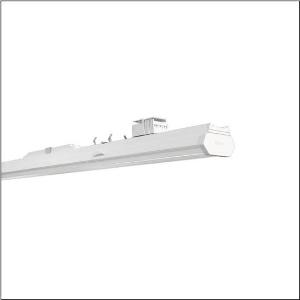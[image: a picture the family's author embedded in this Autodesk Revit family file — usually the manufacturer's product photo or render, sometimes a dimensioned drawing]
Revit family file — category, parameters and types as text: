
# Revit family: licross_21_protected_mo_52td11cn49xg
name_source: partatom
category: Lighting Fixtures
units: mm (PartAtom-declared; Revit-internal decimal feet)

## family parameters
Cut with Voids When Loaded = No
Host = Face
Light Source = No
Part Type = Normal
Room Calculation Point = No
Round Connector Dimension = Use Diameter
Shared = No

## types (1)
- --- (1 x LED, 9070 lm, 50.4 W, 4000K)
    Apparent Load = 50 VA
    CIE Flux Codes = 83 94 98 100 100
    Color Rendering = 80
    Color Temperature = 4000K
    Default Elevation = 1800 mm
    Description = Licross 21 Protected MO, luminaire insert, of sheet steel, galvanised, coil coated, white, length: 1.500mm, width: 90mm, height: 103mm, LED rated luminous flux: 9.080lm, light colour: 840, SDCM (Standard Deviation of Colour Matching)MacAdam ≤ 3 SDCM (initial), control gear: ON/OFF Multilumen, CLOi, with plug, 3-pole, with phase selection, mains connection: 220..240V, AC, 50/60Hz, start of lifetime: 50W, end of service life: 61W, internal wiring halogen-free, primary light control with lens, of plastic, primary optical cover: cover, of PMMA, light emission: direct distribution, primary light characteristic: symmetric, protection rating (complete): IP54, insulation class (complete): insulation class I (protective earthing), certification: CE, ENEC, VDE, UKCA, protection symbol: D if used in an environment with non-conductive dust loads with corresponding accessories, impact resistance: IK06, permissible ambient temperature for indoor applications: -35..+45°C, corresponds to IFS (International Featured Standards) requirements for safety and quality in the food industry, reducing of maximum allowable ambient temperature of 5°C with ceiling mounting, LABS conformity tested according to VDMA 24364:2018-05, The light source and the operating device comply with the requirements of the Ecodesign Regulation (EU) 2019/2020 and are replaceable in accordance with this regulation, packaging unit: 1 piece
    Height = 92 mm
    Lamp = 1 x LED
    Lamp Light Flux = 9070 lm
    Lamp Power = 50.4 W
    Lamp count = 1
    Length = 1500 mm
    Luminous efficacy = 180 lm/W
    Manufacturer = Siteco
    ModVariant = No
    Model = 52TD11CN49XG
    Mounting Place = Ceiling
    Mounting Type = Pendant
    Number of Poles = 1
    OnlyDefault = Yes
    Power Factor = 1
    Product Name = Licross 21 Protected MO
    Product group = luminaire insert | ceiling pendant
    ProductGroupID = 901
    Protection Class = Protection class I
    Protection Degree = IP 54
    RLX_Detail_Level = 1
    RLX_Emergency_Light_Flux = 0 lm
    RLX_Emergency_Type = 0
    RLX_Emergency_Type_DB = No
    RlxData = <blob elided: 22149 chars, md5=94b860a1>
    Socket = socket
    Standby Power = 0 W
    System Light Flux = 9070 lm
    System Power = 50 W
    Type Comments = factory setting: luminous flux: 100 % | (A | C | E) | 117 mA
    Type Image = l_1256148.jpg
    URL = http://relux.com
    VarID = @adj_112381
    Voltage = 0 V
    Weight = 0.00 kg
    Width = 88 mm

## geometry (parser evidence)
native form markers: Blend x4, Sweep x9
no freeform markers — native parametric forms only
